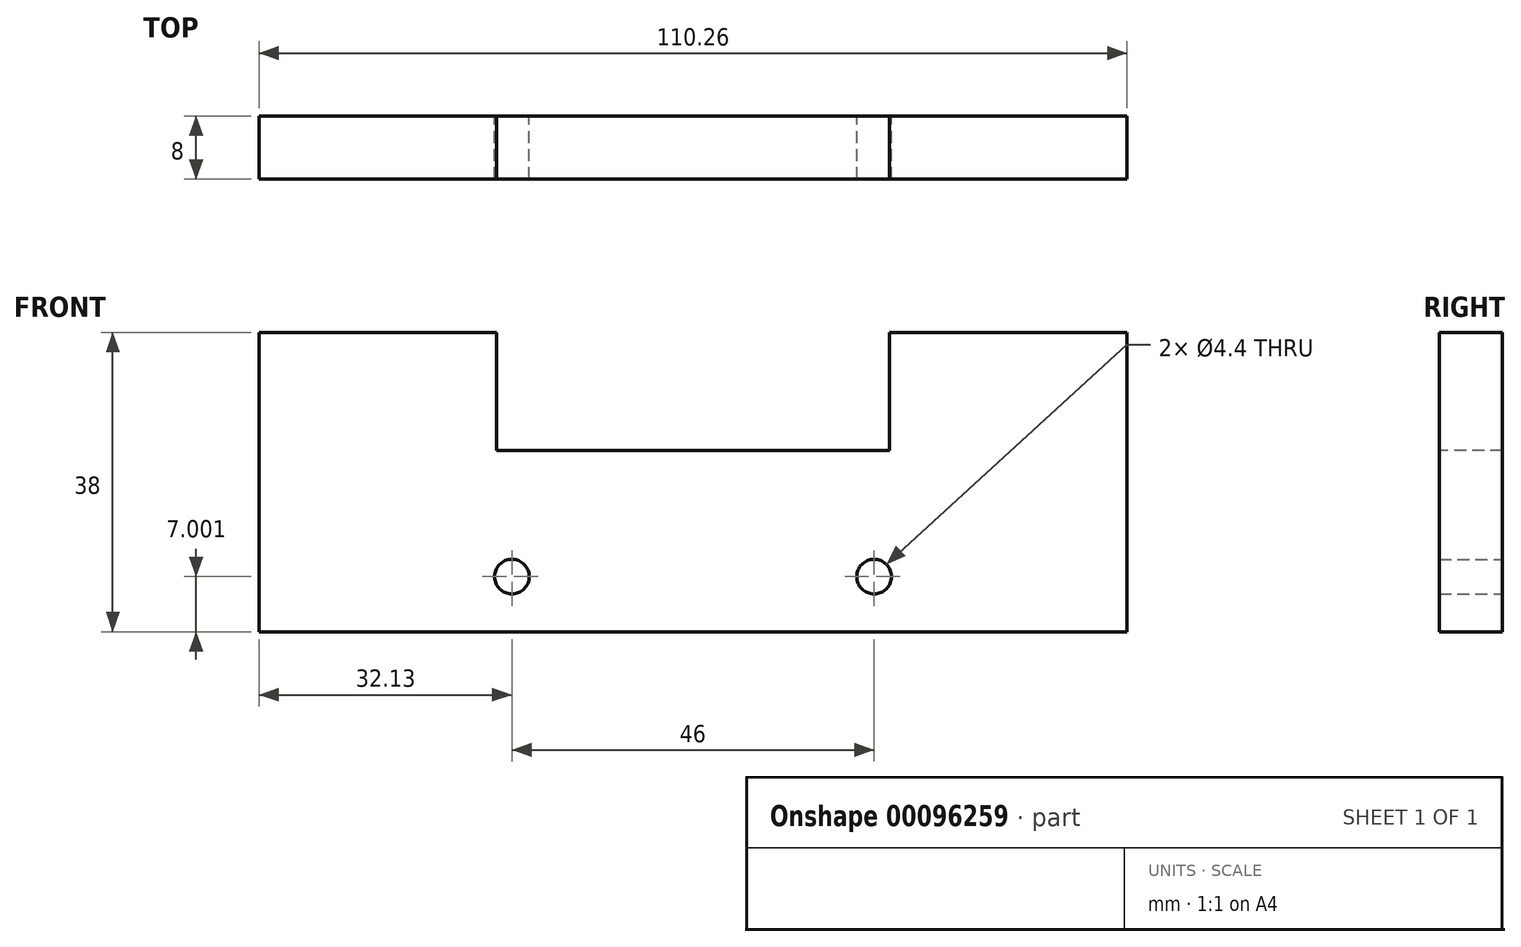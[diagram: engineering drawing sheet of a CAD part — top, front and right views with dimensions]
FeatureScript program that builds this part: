
annotation { "Feature Type Name" : "Feature", "Feature Type Description" : "" }
export const myFeature = defineFeature(function(context is Context, id is Id, definition is map)
    precondition{}
    {
        {
            var Q0;
            Q0=qCreatedBy(makeId("Front.planeOp"),FACE);
            var sketch = newSketch(context, id + "F0", { "sketchPlane" : qUnion([Q0])});
            skLineSegment(sketch, "E0.bottom", {"start": v(-55.13, -17.95) * mm, "end": v(54.87, -17.95) * mm});
            skLineSegment(sketch, "E0.top", {"start": v(-55.13, -55.95) * mm, "end": v(54.87, -55.95) * mm});
            skLineSegment(sketch, "E0.left", {"start": v(-55.13, -17.95) * mm, "end": v(-55.13, -55.95) * mm});
            skLineSegment(sketch, "E0.right", {"start": v(54.87, -17.95) * mm, "end": v(54.87, -55.95) * mm});
            skPoint(sketch, "E1", {"position": v(-23, -48.95) * mm});
            skPoint(sketch, "E2.MirrorP", {"position": v(23, -48.95) * mm});
            skSolve(sketch);
        }
        {
            var Q0;
            Q0=makeQuery(id+"F0.imprint","IMPRINT",FACE,{"disambiguationData":[TD([[makeQuery(id+"F0.imprint","IMPRINT",EDGE,{"derivedFrom":sQuery(id+"F0.wireOp",EDGE,"E0.bottom")}),-1.0]])]});
            extrude(context, id + "F1", {"entities" : qUnion([Q0]), "depth" : 8 * mm});
        }
        {
            var Q0;
            Q0=makeQuery(id+"F1.opExtrude","CAP_FACE",FACE,{"disambiguationData":[OSD([sQuery(id+"F0.wireOp",EDGE,"E0.bottom"),sQuery(id+"F0.wireOp",EDGE,"E0.top"),sQuery(id+"F0.wireOp",EDGE,"E0.left"),sQuery(id+"F0.wireOp",EDGE,"E0.right")])],"isStart":false});
            var sketch = newSketch(context, id + "F2", { "sketchPlane" : qUnion([Q0])});
            skLineSegment(sketch, "E3.bottom", {"start": v(-25.06, -17.95) * mm, "end": v(24.94, -17.95) * mm});
            skLineSegment(sketch, "E3.top", {"start": v(-25.06, -32.95) * mm, "end": v(24.94, -32.95) * mm});
            skLineSegment(sketch, "E3.left", {"start": v(-25.06, -17.95) * mm, "end": v(-25.06, -32.95) * mm});
            skLineSegment(sketch, "E3.right", {"start": v(24.94, -17.95) * mm, "end": v(24.94, -32.95) * mm});
            skSolve(sketch);
        }
        {
            var Q0;
            Q0=makeQuery(id+"F2.imprint","IMPRINT",FACE,{"disambiguationData":[TD([[makeQuery(id+"F2.imprint","IMPRINT",EDGE,{"derivedFrom":sQuery(id+"F2.wireOp",EDGE,"E3.bottom")}),-1.0]])]});
            extrude(context, id + "F3", {"entities" : qUnion([Q0]), "operationType" : NewBodyOperationType.REMOVE, "oppositeDirection" : true, "depth" : 25 * mm});
        }
        {
            var Q0;
            Q0=sQuery(id+"F0.wireOp",VERTEX,"E1");
            var Q1;
            Q1=sQuery(id+"F0.wireOp",VERTEX,"E2.MirrorP");
            var Q2;
            Q2=makeQuery(id+"F1.opExtrude","SWEPT_BODY",BODY,{"disambiguationData":[OSD([sQuery(id+"F0.wireOp",EDGE,"E0.bottom"),sQuery(id+"F0.wireOp",EDGE,"E0.top"),sQuery(id+"F0.wireOp",EDGE,"E0.left"),sQuery(id+"F0.wireOp",EDGE,"E0.right")])]});
            hole(context, id + "F4", {"style" : HoleStyle.SIMPLE, "endStyle" : HoleEndStyle.THROUGH, "oppositeDirection" : true, "standardTappedOrClearance" : lookupTablePath({ "standard" : "ISO", "engagement" : "25%", "pitch" : "0.9 mm", "size" : "M5", "type" : "Tapped" }), "standardBlindInLast" : lookupTablePath({ "standard" : "ISO", "engagement" : "25%", "pitch" : "0.9 mm", "size" : "M5", "type" : "Tapped" }), "holeDiameter" : 4.4 * mm, "locations" : qUnion([Q0, Q1]), "scope" : qUnion([Q2]), "isTappedThrough" : true, "showTappedDepth" : true});
        }
        {
            var Q0;
            Q0=makeQuery(id+"F1.opExtrude","SWEPT_BODY",BODY,{"disambiguationData":[OSD([sQuery(id+"F0.wireOp",EDGE,"E0.bottom"),sQuery(id+"F0.wireOp",EDGE,"E0.top"),sQuery(id+"F0.wireOp",EDGE,"E0.left"),sQuery(id+"F0.wireOp",EDGE,"E0.right")])]});
            var Q1;
            Q1=qCreatedBy(makeId("Right.planeOp"),FACE);
            mirror(context, id + "F5", {"operationType" : NewBodyOperationType.ADD, "entities" : qUnion([Q0]), "mirrorPlane" : qUnion([Q1])});
        }
    });
